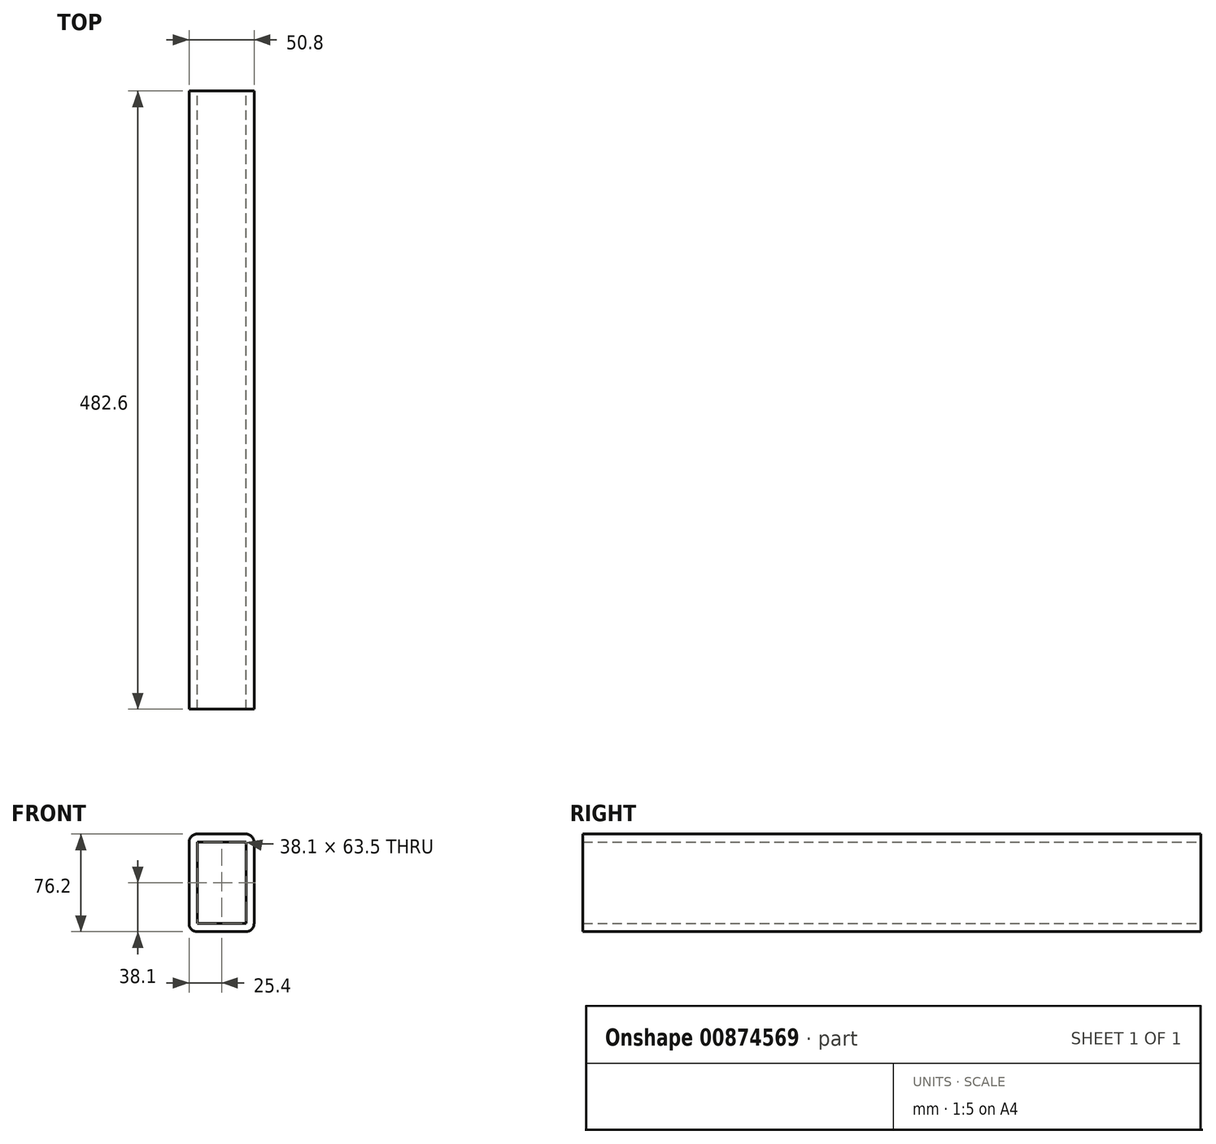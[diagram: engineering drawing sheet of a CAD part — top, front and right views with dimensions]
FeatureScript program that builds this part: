
annotation { "Feature Type Name" : "Feature", "Feature Type Description" : "" }
export const myFeature = defineFeature(function(context is Context, id is Id, definition is map)
    precondition{}
    {
        {
            var Q0;
            Q0=qCreatedBy(makeId("Front.planeOp"),FACE);
            var sketch = newSketch(context, id + "F0", { "sketchPlane" : qUnion([Q0])});
            skLineSegment(sketch, "E0.bottom", {"start": v(-19.05, 38.1) * mm, "end": v(19.05, 38.1) * mm});
            skLineSegment(sketch, "E0.top", {"start": v(-19.05, -38.1) * mm, "end": v(19.05, -38.1) * mm});
            skLineSegment(sketch, "E0.left", {"start": v(-25.4, 31.75) * mm, "end": v(-25.4, -31.75) * mm});
            skLineSegment(sketch, "E0.right", {"start": v(25.4, 31.75) * mm, "end": v(25.4, -31.75) * mm});
            skPoint(sketch, "E0.middle", {"position": v(0, 0) * mm});
            skLineSegment(sketch, "E1.bottom", {"start": v(-19.05, 31.75) * mm, "end": v(19.05, 31.75) * mm});
            skLineSegment(sketch, "E1.top", {"start": v(-19.05, -31.75) * mm, "end": v(19.05, -31.75) * mm});
            skLineSegment(sketch, "E1.left", {"start": v(-19.05, 31.75) * mm, "end": v(-19.05, -31.75) * mm});
            skLineSegment(sketch, "E1.right", {"start": v(19.05, 31.75) * mm, "end": v(19.05, -31.75) * mm});
            skPoint(sketch, "E2.visualSharp", {"position": v(-25.4, 38.1) * mm});
            skArc(sketch, "E2.filletArc", {"start": v(-19.05, 38.1) * mm, "mid": v(-23.54, 36.24) * mm, "end": v(-25.4, 31.75) * mm});
            skPoint(sketch, "E3.visualSharp", {"position": v(25.4, 38.1) * mm});
            skArc(sketch, "E3.filletArc", {"start": v(25.4, 31.75) * mm, "mid": v(23.54, 36.24) * mm, "end": v(19.05, 38.1) * mm});
            skPoint(sketch, "E4.visualSharp", {"position": v(25.4, -38.1) * mm});
            skArc(sketch, "E4.filletArc", {"start": v(19.05, -38.1) * mm, "mid": v(23.54, -36.24) * mm, "end": v(25.4, -31.75) * mm});
            skPoint(sketch, "E5.visualSharp", {"position": v(-25.4, -38.1) * mm});
            skArc(sketch, "E5.filletArc", {"start": v(-25.4, -31.75) * mm, "mid": v(-23.54, -36.24) * mm, "end": v(-19.05, -38.1) * mm});
            skSolve(sketch);
        }
        {
            var Q0;
            Q0=makeQuery(id+"F0.imprint","IMPRINT",FACE,{"disambiguationData":[TD([[makeQuery(id+"F0.imprint","IMPRINT",EDGE,{"derivedFrom":sQuery(id+"F0.wireOp",EDGE,"E0.bottom")}),-1.0]])]});
            extrude(context, id + "F1", {"entities" : qUnion([Q0]), "depth" : 482.6 * mm, "offsetDistance" : 25.4 * mm});
        }
    });
